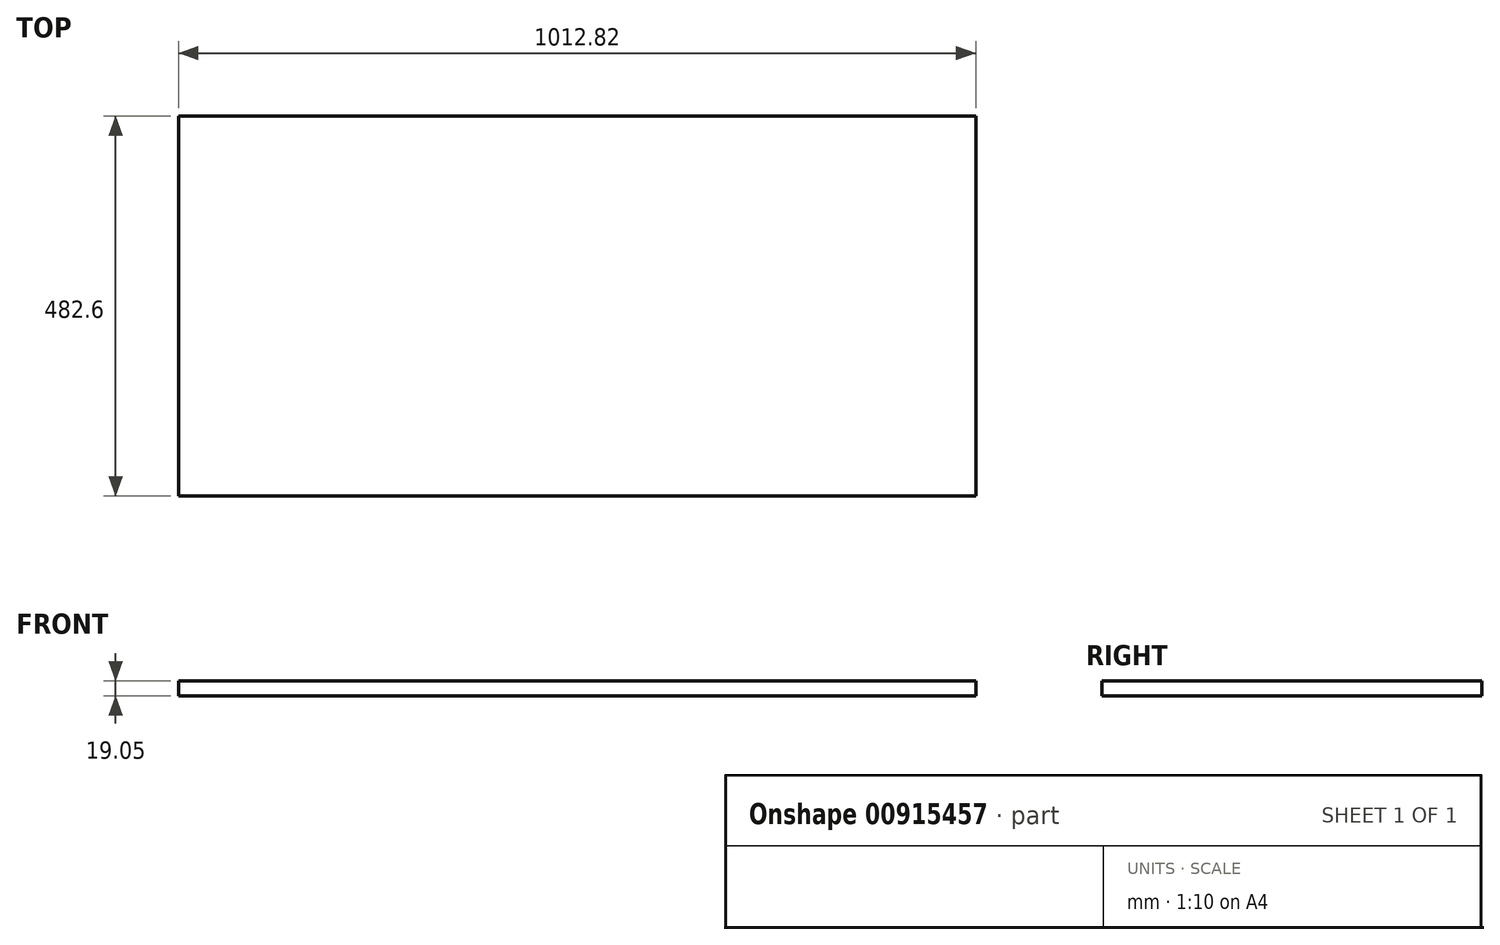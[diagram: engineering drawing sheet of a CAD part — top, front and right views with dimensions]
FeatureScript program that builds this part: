
annotation { "Feature Type Name" : "Feature", "Feature Type Description" : "" }
export const myFeature = defineFeature(function(context is Context, id is Id, definition is map)
    precondition{}
    {
        {
            var Q0;
            Q0=qCreatedBy(makeId("Top.planeOp"),FACE);
            var sketch = newSketch(context, id + "F0", { "sketchPlane" : qUnion([Q0])});
            skLineSegment(sketch, "E0.bottom", {"start": v(506.41, 241.3) * mm, "end": v(-506.41, 241.3) * mm});
            skLineSegment(sketch, "E0.top", {"start": v(506.41, -241.3) * mm, "end": v(-506.41, -241.3) * mm});
            skLineSegment(sketch, "E0.left", {"start": v(506.41, 241.3) * mm, "end": v(506.41, -241.3) * mm});
            skLineSegment(sketch, "E0.right", {"start": v(-506.41, 241.3) * mm, "end": v(-506.41, -241.3) * mm});
            skPoint(sketch, "E0.middle", {"position": v(0, 0) * mm});
            skSolve(sketch);
        }
        {
            var Q0;
            Q0=makeQuery(id+"F0.imprint","IMPRINT",FACE,{"disambiguationData":[TD([[makeQuery(id+"F0.imprint","IMPRINT",EDGE,{"derivedFrom":sQuery(id+"F0.wireOp",EDGE,"E0.bottom")}),1.0]])]});
            extrude(context, id + "F1", {"entities" : qUnion([Q0]), "depth" : 19.05 * mm, "offsetDistance" : 25.4 * mm});
        }
    });
